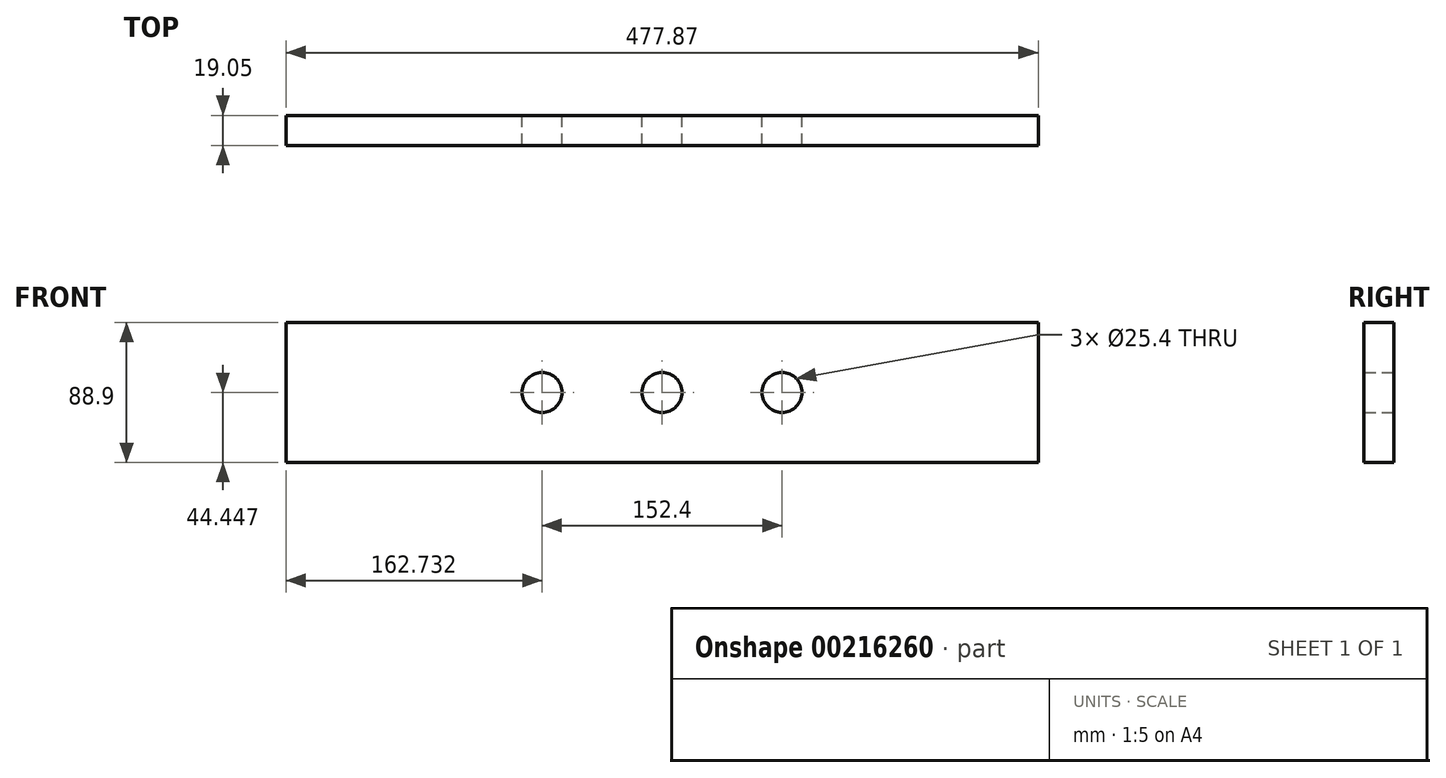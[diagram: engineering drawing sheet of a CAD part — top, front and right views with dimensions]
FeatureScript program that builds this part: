
annotation { "Feature Type Name" : "Feature", "Feature Type Description" : "" }
export const myFeature = defineFeature(function(context is Context, id is Id, definition is map)
    precondition{}
    {
        {
            var Q0;
            Q0=qCreatedBy(makeId("Front.planeOp"),FACE);
            var sketch = newSketch(context, id + "F0", { "sketchPlane" : qUnion([Q0])});
            skLineSegment(sketch, "E0", {"start": v(-3047.98, -2233.2) * mm, "end": v(-2570.11, -2233.2) * mm});
            skLineSegment(sketch, "E1", {"start": v(-2570.11, -2233.2) * mm, "end": v(-2570.11, -2322.1) * mm});
            skLineSegment(sketch, "E2", {"start": v(-2570.11, -2322.1) * mm, "end": v(-3047.98, -2322.1) * mm});
            skLineSegment(sketch, "E3", {"start": v(-3047.98, -2322.1) * mm, "end": v(-3047.98, -2233.2) * mm});
            skCircle(sketch, "E4", {"center": v(-2732.85, -2277.64) * mm, "radius": 12.7 * mm});
            skCircle(sketch, "E5", {"center": v(-2809.05, -2277.64) * mm, "radius": 12.7 * mm});
            skCircle(sketch, "E6", {"center": v(-2885.25, -2277.64) * mm, "radius": 12.7 * mm});
            skLineSegment(sketch, "E7", {"start": v(-3047.98, -2277.64) * mm, "end": v(-2570.11, -2277.64) * mm, "construction": true});
            skSolve(sketch);
        }
        {
            var Q0;
            Q0=makeQuery(id+"F0.imprint","IMPRINT",FACE,{"disambiguationData":[TD([[makeQuery(id+"F0.imprint","IMPRINT",EDGE,{"derivedFrom":sQuery(id+"F0.wireOp",EDGE,"E0")}),-1.0]])]});
            extrude(context, id + "F1", {"entities" : qUnion([Q0]), "depth" : 19.05 * mm});
        }
    });
